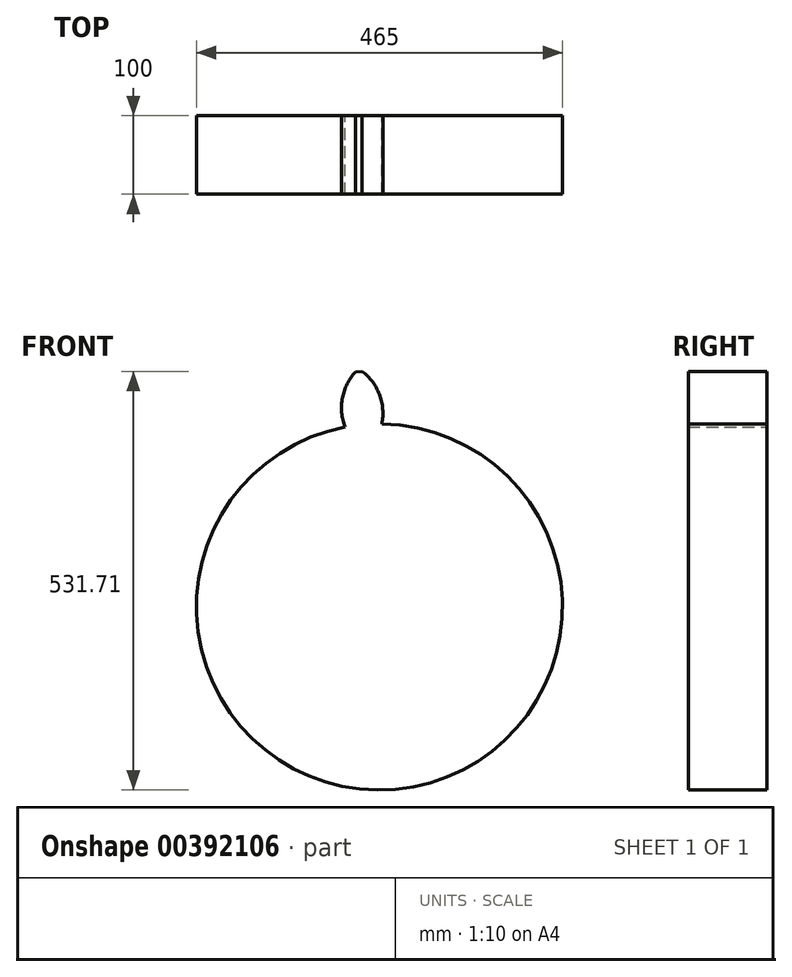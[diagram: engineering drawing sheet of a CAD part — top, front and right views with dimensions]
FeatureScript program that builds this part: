
annotation { "Feature Type Name" : "Feature", "Feature Type Description" : "" }
export const myFeature = defineFeature(function(context is Context, id is Id, definition is map)
    precondition{}
    {
        {
            var Q0;
            Q0=qCreatedBy(makeId("Front.planeOp"),FACE);
            var sketch = newSketch(context, id + "F0", { "sketchPlane" : qUnion([Q0])});
            skCircle(sketch, "E0", {"center": v(0, 0) * mm, "radius": 232.5 * mm});
            skCircle(sketch, "E1", {"center": v(0, 0) * mm, "radius": 270 * mm, "construction": true});
            skCircle(sketch, "E2", {"center": v(0, 0) * mm, "radius": 300 * mm, "construction": true});
            skLineSegment(sketch, "E3", {"start": v(0, 114.52) * mm, "end": v(0, 1000) * mm, "construction": true});
            skLineSegment(sketch, "E4", {"start": v(-9.98, 114.08) * mm, "end": v(-88.95, 1016.74) * mm, "construction": true});
            skArc(sketch, "E5.filletArc", {"start": v(-9.98, 114.08) * mm, "mid": v(-4.78, 109.52) * mm, "end": v(0, 114.52) * mm, "construction": true});
            skLineSegment(sketch, "E6", {"start": v(0, 270) * mm, "end": v(-1000, 270) * mm, "construction": true});
            skLineSegment(sketch, "E7", {"start": v(0, 270) * mm, "end": v(-741.82, 0) * mm});
            skCircle(sketch, "E8", {"center": v(0, 270) * mm, "radius": 67.5 * mm, "construction": true});
            skCircle(sketch, "E9", {"center": v(0, 0) * mm, "radius": 253.72 * mm, "construction": true});
            skCircle(sketch, "E10", {"center": v(-63, 245.77) * mm, "radius": 67.5 * mm, "construction": true});
            skArc(sketch, "E11", {"start": v(0, 270) * mm, "mid": v(-8.87, 286.1) * mm, "end": v(-21.76, 299.2) * mm});
            skArc(sketch, "E12", {"start": v(3.18, 232.48) * mm, "mid": v(4.26, 251.47) * mm, "end": v(0, 270) * mm});
            skArc(sketch, "E13.MirrorCS", {"start": v(-46.89, 265.9) * mm, "mid": v(-40.94, 283.3) * mm, "end": v(-30.52, 298.44) * mm});
            skArc(sketch, "E14.MirrorCS", {"start": v(-43.5, 228.4) * mm, "mid": v(-47.86, 246.9) * mm, "end": v(-46.89, 265.9) * mm});
            skLineSegment(sketch, "E15", {"start": v(-30.52, 298.44) * mm, "end": v(-21.76, 299.2) * mm});
            skSolve(sketch);
        }
        {
            var Q0;
            {var subQ0=sQuery(id+"F0.wireOp",EDGE,"E0");var subQ1=makeQuery(id+"F0.imprint","INTERSECT",VERTEX,{"derivedFrom":[subQ0,sQuery(id+"F0.wireOp",EDGE,"E12")]});Q0=makeQuery(id+"F0.imprint","IMPRINT",FACE,{"disambiguationData":[TD([[makeQuery(id+"F0.imprint","IMPRINT",EDGE,{"disambiguationData":[TD([[subQ1,-1.0]])],"derivedFrom":subQ0}),1.0]])]});}
            var Q1;
            {var subQ0=sQuery(id+"F0.wireOp",EDGE,"E12");Q1=makeQuery(id+"F0.imprint","IMPRINT",FACE,{"disambiguationData":[TD([[makeQuery(id+"F0.imprint","IMPRINT",EDGE,{"derivedFrom":subQ0}),1.0]])]});}
            var Q2;
            {var subQ1=sQuery(id+"F0.wireOp",EDGE,"E11");Q2=makeQuery(id+"F0.imprint","IMPRINT",FACE,{"disambiguationData":[TD([[makeQuery(id+"F0.imprint","IMPRINT",EDGE,{"derivedFrom":subQ1}),1.0]])]});}
            extrude(context, id + "F1", {"entities" : qUnion([Q0, Q1, Q2]), "depth" : 100 * mm});
        }
    });
